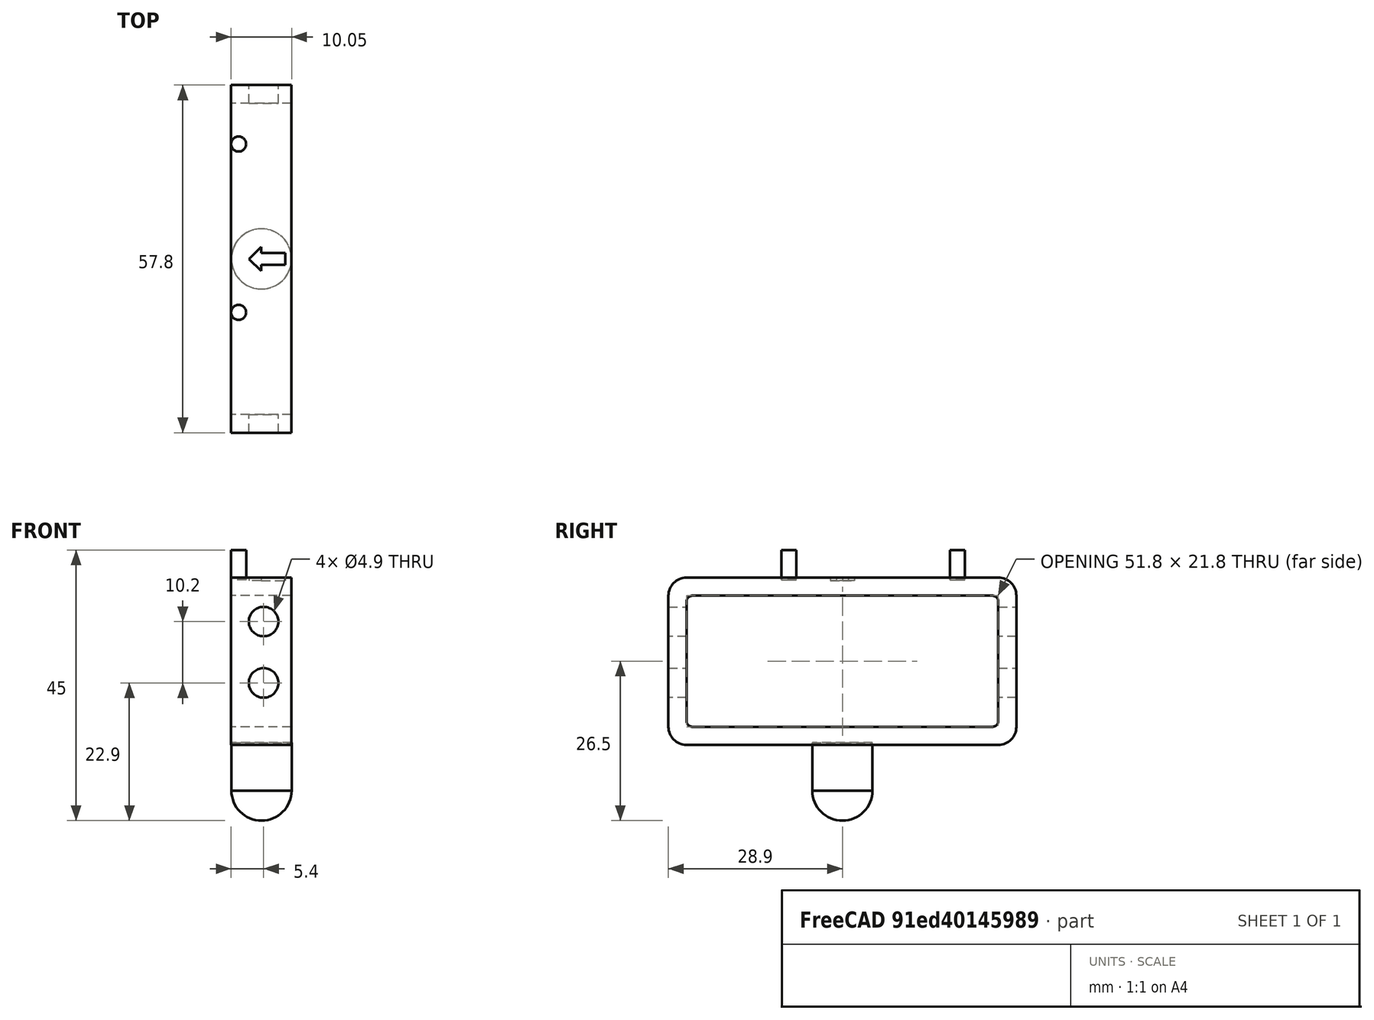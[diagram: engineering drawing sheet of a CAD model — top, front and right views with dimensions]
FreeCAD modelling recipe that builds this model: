
FCSTD DOCUMENT  (FreeCAD 0.17R13541 (Git))
Label: icelobot_f
License: All rights reserved
LicenseURL: http://en.wikipedia.org/wiki/All_rights_reserved
objects: Part::Cylinder×3, Part::Feature×1, Part::Sphere×1, Part::Box×1, Part::Cut×1
note: 7 computed .brp shape members not serialized (recipe doc carries the construction recipe); baked Part::Feature solids carry a one-line shape summary decoded from their .brp

FEATURE [Part::Cylinder] Cylinder002  label="Cilindrof1"
  Angle = 360
  AttacherType = Attacher::AttachEngine3D
  Height = 5
  Placement = pos=(-39.8,-15.9,-33) rot=(0,0,1;0rad)
  Radius = 1.25
FEATURE [Part::Cylinder] Cylinder003  label="Cilindrof2"
  Angle = 360
  AttacherType = Attacher::AttachEngine3D
  Height = 5
  Placement = pos=(-39.8,-43.9,-33) rot=(0,0,1;0rad)
  Radius = 1.25
FEATURE [Part::Feature] Part__Feature001  label="front"
  Placement = pos=(-31.5,-35,-45) rot=(-0.707107,0,0.707107;3.14159rad)
  shape: bbox 10 x 57.8 x 27.8 mm, 30 faces (baked)
FEATURE [Part::Sphere] Sphere  label="Esfera"
  Angle1 = -90
  Angle2 = 90
  Angle3 = 360
  AttacherType = Attacher::AttachEngine3D
  Radius = 5
FEATURE [Part::Box] Box002  label="Cubo002"
  AttacherType = Attacher::AttachEngine3D
  Height = 10
  Length = 10
  Placement = pos=(-5,-5,0) rot=(0,0,1;0rad)
  Width = 10
FEATURE [Part::Cut] Cut
  Base = -> Sphere
  Placement = pos=(-36,-35,-68) rot=(0,0,1;0rad)
  Tool = -> Box002
FEATURE [Part::Cylinder] Cylinder004  label="Cilindro"
  Angle = 360
  AttacherType = Attacher::AttachEngine3D
  Height = 8
  Placement = pos=(-36,-35,-68) rot=(0,0,1;0rad)
  Radius = 5
